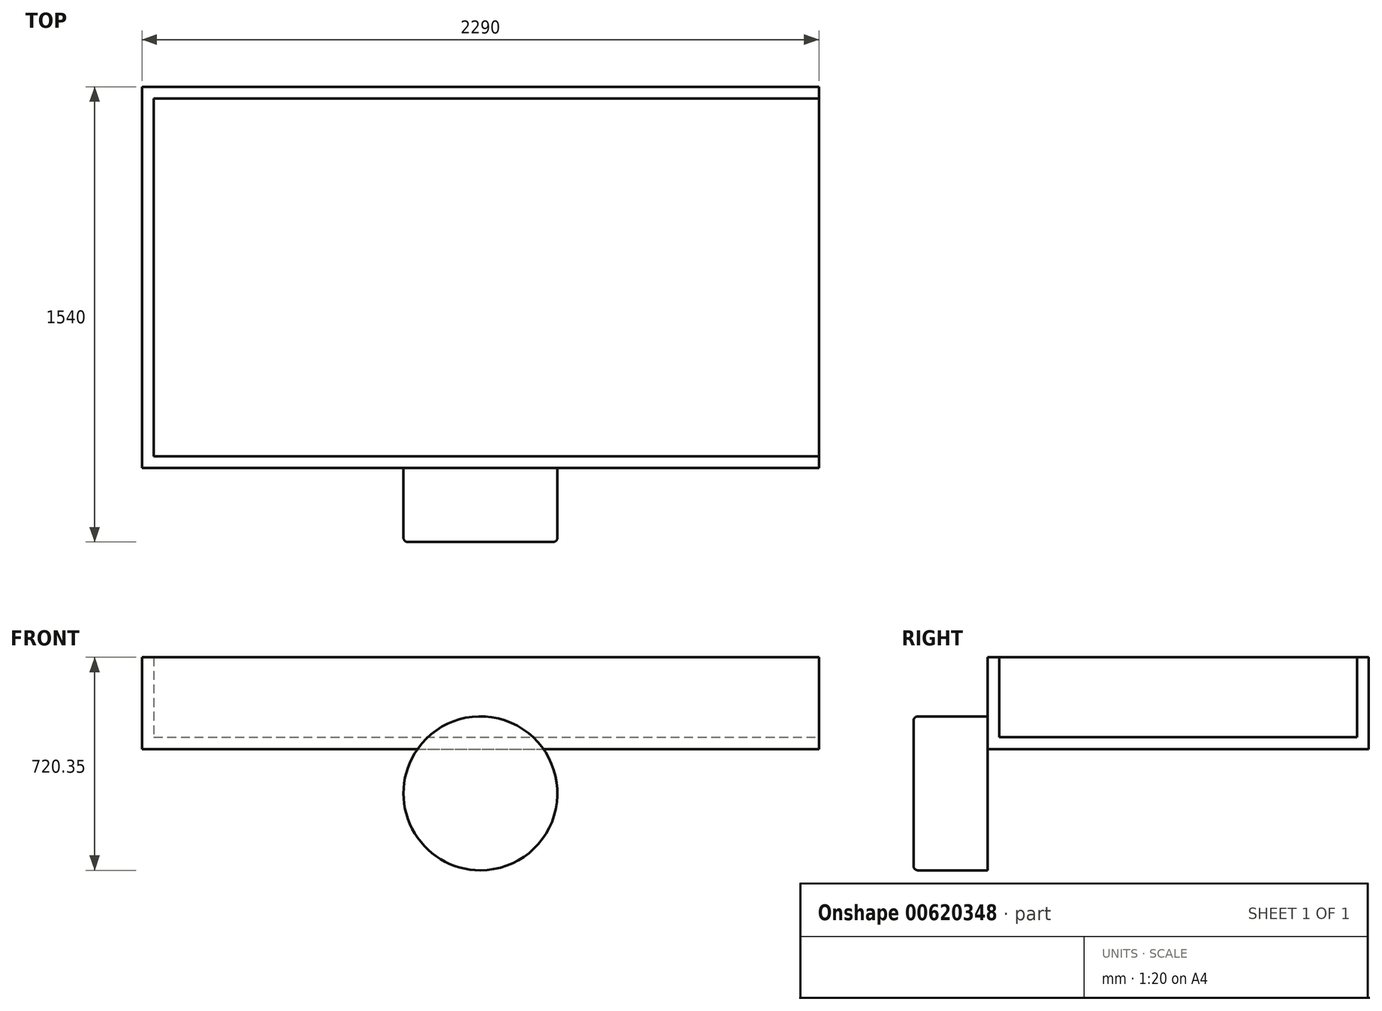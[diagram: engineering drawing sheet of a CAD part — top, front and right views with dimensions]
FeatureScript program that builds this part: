
annotation { "Feature Type Name" : "Feature", "Feature Type Description" : "" }
export const myFeature = defineFeature(function(context is Context, id is Id, definition is map)
    precondition{}
    {
        {
            var Q0;
            Q0=qCreatedBy(makeId("Top.planeOp"),FACE);
            var sketch = newSketch(context, id + "F0", { "sketchPlane" : qUnion([Q0])});
            skLineSegment(sketch, "E0.bottom", {"start": v(-1145, 645) * mm, "end": v(1145, 645) * mm});
            skLineSegment(sketch, "E0.top", {"start": v(-1145, -645) * mm, "end": v(1145, -645) * mm});
            skLineSegment(sketch, "E0.left", {"start": v(-1145, 645) * mm, "end": v(-1145, -645) * mm});
            skLineSegment(sketch, "E0.right", {"start": v(1145, 645) * mm, "end": v(1145, -645) * mm});
            skPoint(sketch, "E0.middle", {"position": v(0, 0) * mm});
            skSolve(sketch);
        }
        {
            var Q0;
            Q0=makeQuery(id+"F0.imprint","IMPRINT",FACE,{"disambiguationData":[TD([[makeQuery(id+"F0.imprint","IMPRINT",EDGE,{"derivedFrom":sQuery(id+"F0.wireOp",EDGE,"E0.bottom")}),-1.0]])]});
            extrude(context, id + "F1", {"entities" : qUnion([Q0]), "depth" : 310 * mm, "offsetDistance" : 25 * mm});
        }
        {
            var Q0;
            Q0=makeQuery(id+"F1.opExtrude","CAP_FACE",FACE,{"disambiguationData":[OSD([sQuery(id+"F0.wireOp",EDGE,"E0.bottom"),sQuery(id+"F0.wireOp",EDGE,"E0.top"),sQuery(id+"F0.wireOp",EDGE,"E0.left"),sQuery(id+"F0.wireOp",EDGE,"E0.right")])],"isStart":false});
            var Q1;
            Q1=makeQuery(id+"F1.opExtrude","SWEPT_FACE",FACE,{"disambiguationData":[OSD([sQuery(id+"F0.wireOp",EDGE,"E0.right")])]});
            shell(context, id + "F2", {"entities" : qUnion([Q0, Q1]), "thickness" : 40 * mm});
        }
        {
            var Q0;
            Q0=makeQuery(id+"F1.opExtrude","SWEPT_FACE",FACE,{"disambiguationData":[OSD([sQuery(id+"F0.wireOp",EDGE,"E0.top")])]});
            var sketch = newSketch(context, id + "F3", { "sketchPlane" : qUnion([Q0])});
            skCircle(sketch, "E1", {"center": v(0, -150) * mm, "radius": 260.35 * mm});
            skLineSegment(sketch, "E2", {"start": v(0, 0) * mm, "end": v(0, -150) * mm, "construction": true});
            skPoint(sketch, "E2.endSnap0", {"position": v(0, 0) * mm});
            skSolve(sketch);
        }
        {
            var Q0;
            {var subQ0=sQuery(id+"F3.wireOp",EDGE,"E1");var subQ1=makeQuery(id+"F1.opExtrude","CAP_EDGE",EDGE,{"disambiguationData":[OSD([sQuery(id+"F0.wireOp",EDGE,"E0.top")])],"isStart":true});var subQ2=makeQuery(id+"F3.imprint","INTERSECT",VERTEX,{"disambiguationData":[OD(0.0)],"derivedFrom":[subQ1,subQ0]});Q0=makeQuery(id+"F3.imprint","IMPRINT",FACE,{"disambiguationData":[TD([[makeQuery(id+"F3.imprint","IMPRINT",EDGE,{"disambiguationData":[TD([[subQ2,-1.0]])],"derivedFrom":subQ0}),1.0]])]});}
            var Q1;
            {var subQ0=sQuery(id+"F3.wireOp",EDGE,"E1");var subQ1=makeQuery(id+"F1.opExtrude","CAP_EDGE",EDGE,{"disambiguationData":[OSD([sQuery(id+"F0.wireOp",EDGE,"E0.top")])],"isStart":true});var subQ2=makeQuery(id+"F3.imprint","INTERSECT",VERTEX,{"disambiguationData":[OD(0.0)],"derivedFrom":[subQ1,subQ0]});Q1=makeQuery(id+"F3.imprint","IMPRINT",FACE,{"disambiguationData":[TD([[makeQuery(id+"F3.imprint","IMPRINT",EDGE,{"disambiguationData":[TD([[subQ2,1.0]])],"derivedFrom":subQ0}),1.0]])]});}
            extrude(context, id + "F4", {"entities" : qUnion([Q0, Q1]), "operationType" : NewBodyOperationType.ADD, "depth" : 250 * mm, "offsetDistance" : 25 * mm});
        }
        {
            var Q0;
            Q0=makeQuery(id+"F4.opExtrude","CAP_EDGE",EDGE,{"disambiguationData":[OSD([sQuery(id+"F3.wireOp",EDGE,"E1")])],"isStart":false});
            fillet(context, id + "F5", {"entities" : qUnion([Q0]), "radius" : 15 * mm, "tangentPropagation" : true, "allowEdgeOverflow" : false});
        }
    });
